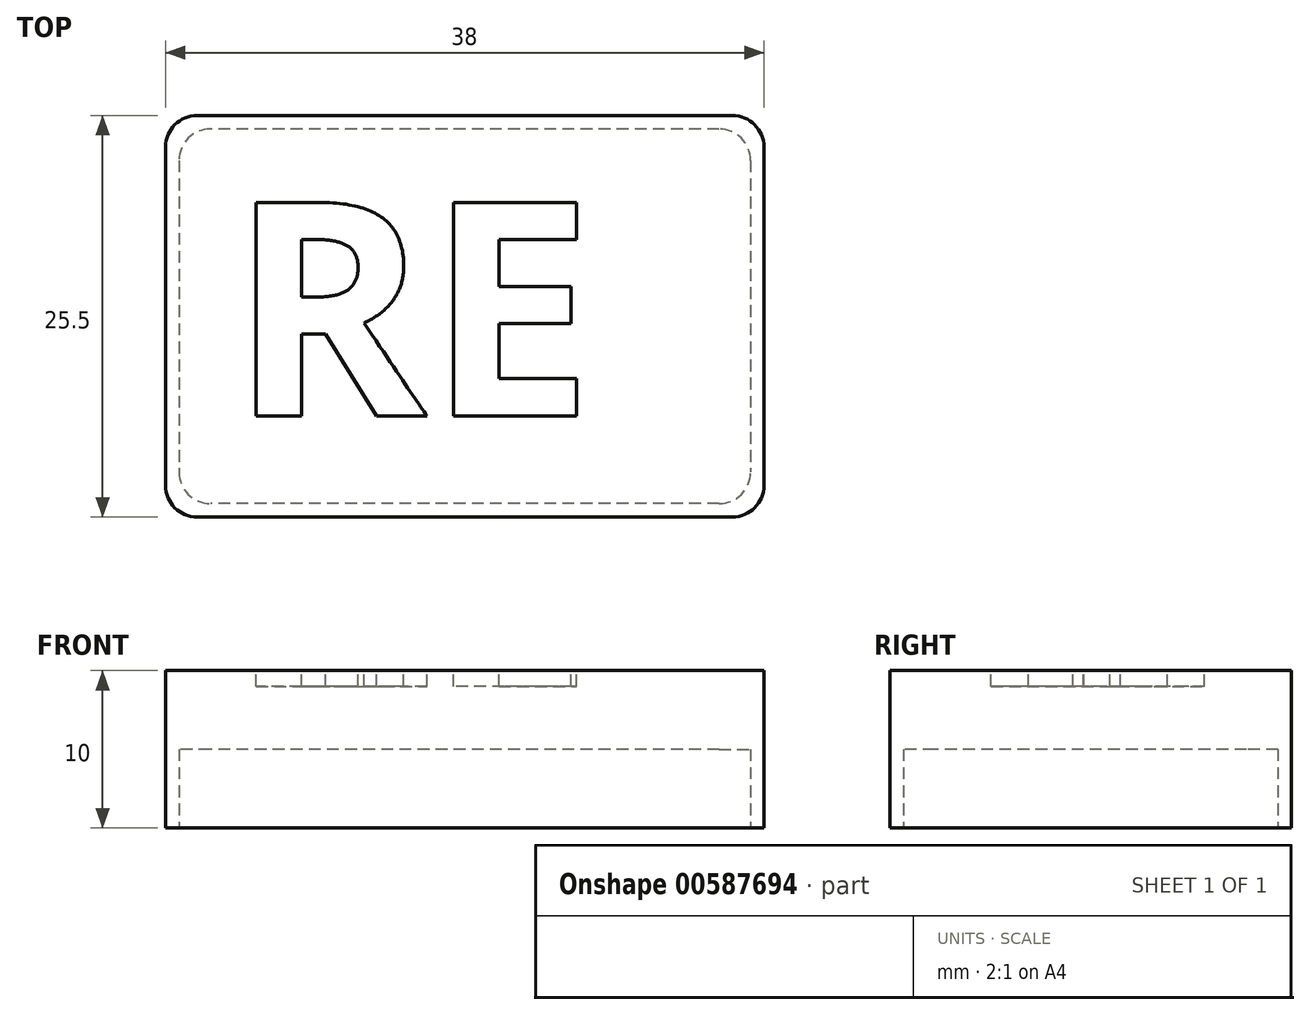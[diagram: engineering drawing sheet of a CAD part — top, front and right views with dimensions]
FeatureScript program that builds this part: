
annotation { "Feature Type Name" : "Feature", "Feature Type Description" : "" }
export const myFeature = defineFeature(function(context is Context, id is Id, definition is map)
    precondition{}
    {
        {
            var Q0;
            Q0=qCreatedBy(makeId("Top.planeOp"),FACE);
            var sketch = newSketch(context, id + "F0", { "sketchPlane" : qUnion([Q0])});
            skLineSegment(sketch, "E0.bottom", {"start": v(-19, -12.75) * mm, "end": v(19, -12.75) * mm});
            skLineSegment(sketch, "E0.top", {"start": v(-19, 12.75) * mm, "end": v(19, 12.75) * mm});
            skLineSegment(sketch, "E0.left", {"start": v(-19, -12.75) * mm, "end": v(-19, 12.75) * mm});
            skLineSegment(sketch, "E0.right", {"start": v(19, -12.75) * mm, "end": v(19, 12.75) * mm});
            skPoint(sketch, "E0.middle", {"position": v(0, 0) * mm});
            skSolve(sketch);
        }
        {
            var Q0;
            Q0=makeQuery(id+"F0.imprint","IMPRINT",FACE,{"disambiguationData":[TD([[makeQuery(id+"F0.imprint","IMPRINT",EDGE,{"derivedFrom":sQuery(id+"F0.wireOp",EDGE,"E0.bottom")}),1.0]])]});
            extrude(context, id + "F1", {"entities" : qUnion([Q0]), "oppositeDirection" : true, "depth" : 10 * mm, "offsetDistance" : 25 * mm});
        }
        {
            var Q0;
            Q0=makeQuery(id+"F1.opExtrude","CAP_FACE",FACE,{"disambiguationData":[OSD([sQuery(id+"F0.wireOp",EDGE,"E0.bottom"),sQuery(id+"F0.wireOp",EDGE,"E0.top"),sQuery(id+"F0.wireOp",EDGE,"E0.left"),sQuery(id+"F0.wireOp",EDGE,"E0.right")])],"isStart":false});
            var sketch = newSketch(context, id + "F2", { "sketchPlane" : qUnion([Q0])});
            skLineSegment(sketch, "E1.bottom", {"start": v(18.15, -11.9) * mm, "end": v(-18.15, -11.9) * mm});
            skLineSegment(sketch, "E1.top", {"start": v(18.15, 11.9) * mm, "end": v(-18.15, 11.9) * mm});
            skLineSegment(sketch, "E1.left", {"start": v(18.15, -11.9) * mm, "end": v(18.15, 11.9) * mm});
            skLineSegment(sketch, "E1.right", {"start": v(-18.15, -11.9) * mm, "end": v(-18.15, 11.9) * mm});
            skPoint(sketch, "E1.middle", {"position": v(0, 0) * mm});
            skSolve(sketch);
        }
        {
            var Q0;
            Q0=makeQuery(id+"F2.imprint","IMPRINT",FACE,{"disambiguationData":[TD([[makeQuery(id+"F2.imprint","IMPRINT",EDGE,{"derivedFrom":sQuery(id+"F2.wireOp",EDGE,"E1.bottom")}),-1.0]])]});
            extrude(context, id + "F3", {"entities" : qUnion([Q0]), "operationType" : NewBodyOperationType.REMOVE, "oppositeDirection" : true, "depth" : 5 * mm, "offsetDistance" : 25 * mm});
        }
        {
            var Q0;
            Q0=makeQuery(id+"F1.opExtrude","CAP_FACE",FACE,{"disambiguationData":[OSD([sQuery(id+"F0.wireOp",EDGE,"E0.bottom"),sQuery(id+"F0.wireOp",EDGE,"E0.top"),sQuery(id+"F0.wireOp",EDGE,"E0.left"),sQuery(id+"F0.wireOp",EDGE,"E0.right")])],"isStart":true});
            var sketch = newSketch(context, id + "F4", { "sketchPlane" : qUnion([Q0])});
            skText(sketch, "E2", { "text": "SCREWS", "fontName": "OpenSans-Bold.ttf"});
            const initialGuessF4  = {"E2": [-0.0375, -0.00632, 1, 0, 0.01367]};
            skSetInitialGuess(sketch, initialGuessF4);
            skSolve(sketch);
        }
        {
            var Q0;
            Q0=makeQuery(id+"F4.imprint","IMPRINT",FACE,{"disambiguationData":[TD([[makeQuery(id+"F4.imprint","IMPRINT",EDGE,{"derivedFrom":sQuery(id+"F4.wireOp",EDGE,"E2.sketch_text.stroke-0")}),-1.0]])]});
            var Q1;
            Q1=makeQuery(id+"F4.imprint","IMPRINT",FACE,{"disambiguationData":[TD([[makeQuery(id+"F4.imprint","IMPRINT",EDGE,{"derivedFrom":sQuery(id+"F4.wireOp",EDGE,"E2.sketch_text.stroke-28")}),-1.0]])]});
            var Q2;
            Q2=makeQuery(id+"F4.imprint","IMPRINT",FACE,{"disambiguationData":[TD([[makeQuery(id+"F4.imprint","IMPRINT",EDGE,{"derivedFrom":sQuery(id+"F4.wireOp",EDGE,"E2.sketch_text.stroke-43")}),-1.0]])]});
            var Q3;
            Q3=makeQuery(id+"F4.imprint","IMPRINT",FACE,{"disambiguationData":[TD([[makeQuery(id+"F4.imprint","IMPRINT",EDGE,{"derivedFrom":sQuery(id+"F4.wireOp",EDGE,"E2.sketch_text.stroke-62")}),-1.0]])]});
            var Q4;
            Q4=makeQuery(id+"F4.imprint","IMPRINT",FACE,{"disambiguationData":[TD([[makeQuery(id+"F4.imprint","IMPRINT",EDGE,{"derivedFrom":sQuery(id+"F4.wireOp",EDGE,"E2.sketch_text.stroke-74")}),-1.0]])]});
            var Q5;
            Q5=makeQuery(id+"F4.imprint","IMPRINT",FACE,{"disambiguationData":[TD([[makeQuery(id+"F4.imprint","IMPRINT",EDGE,{"derivedFrom":sQuery(id+"F4.wireOp",EDGE,"E2.sketch_text.stroke-98")}),-1.0]])]});
            extrude(context, id + "F5", {"entities" : qUnion([Q0, Q1, Q2, Q3, Q4, Q5]), "operationType" : NewBodyOperationType.REMOVE, "oppositeDirection" : true, "depth" : 1 * mm, "offsetDistance" : 25 * mm});
        }
        {
            var Q0;
            Q0=makeQuery(id+"F1.opExtrude","SWEPT_EDGE",EDGE,{"disambiguationData":[OSD([sQuery(id+"F0.wireOp",EDGE,"E0.bottom"),sQuery(id+"F0.wireOp",EDGE,"E0.left")])]});
            var Q1;
            Q1=makeQuery(id+"F1.opExtrude","SWEPT_EDGE",EDGE,{"disambiguationData":[OSD([sQuery(id+"F0.wireOp",EDGE,"E0.bottom"),sQuery(id+"F0.wireOp",EDGE,"E0.right")])]});
            var Q2;
            Q2=makeQuery(id+"F1.opExtrude","SWEPT_EDGE",EDGE,{"disambiguationData":[OSD([sQuery(id+"F0.wireOp",EDGE,"E0.top"),sQuery(id+"F0.wireOp",EDGE,"E0.right")])]});
            var Q3;
            Q3=makeQuery(id+"F1.opExtrude","SWEPT_EDGE",EDGE,{"disambiguationData":[OSD([sQuery(id+"F0.wireOp",EDGE,"E0.top"),sQuery(id+"F0.wireOp",EDGE,"E0.left")])]});
            fillet(context, id + "F6", {"entities" : qUnion([Q0, Q1, Q2, Q3]), "radius" : 2 * mm, "tangentPropagation" : true, "allowEdgeOverflow" : false});
        }
        {
            var Q0;
            Q0=makeQuery(id+"F3.boolean.opBoolean","COPY",EDGE,{"derivedFrom":makeQuery(id+"F3.opExtrude","SWEPT_EDGE",EDGE,{"disambiguationData":[OSD([sQuery(id+"F2.wireOp",EDGE,"E1.top"),sQuery(id+"F2.wireOp",EDGE,"E1.left")])]})});
            var Q1;
            Q1=makeQuery(id+"F3.boolean.opBoolean","COPY",EDGE,{"derivedFrom":makeQuery(id+"F3.opExtrude","SWEPT_EDGE",EDGE,{"disambiguationData":[OSD([sQuery(id+"F2.wireOp",EDGE,"E1.top"),sQuery(id+"F2.wireOp",EDGE,"E1.right")])]})});
            var Q2;
            Q2=makeQuery(id+"F3.boolean.opBoolean","COPY",EDGE,{"derivedFrom":makeQuery(id+"F3.opExtrude","SWEPT_EDGE",EDGE,{"disambiguationData":[OSD([sQuery(id+"F2.wireOp",EDGE,"E1.bottom"),sQuery(id+"F2.wireOp",EDGE,"E1.right")])]})});
            var Q3;
            Q3=makeQuery(id+"F3.boolean.opBoolean","COPY",EDGE,{"derivedFrom":makeQuery(id+"F3.opExtrude","SWEPT_EDGE",EDGE,{"disambiguationData":[OSD([sQuery(id+"F2.wireOp",EDGE,"E1.bottom"),sQuery(id+"F2.wireOp",EDGE,"E1.left")])]})});
            fillet(context, id + "F7", {"entities" : qUnion([Q0, Q1, Q2, Q3]), "radius" : 2 * mm, "tangentPropagation" : true, "allowEdgeOverflow" : false});
        }
    });
